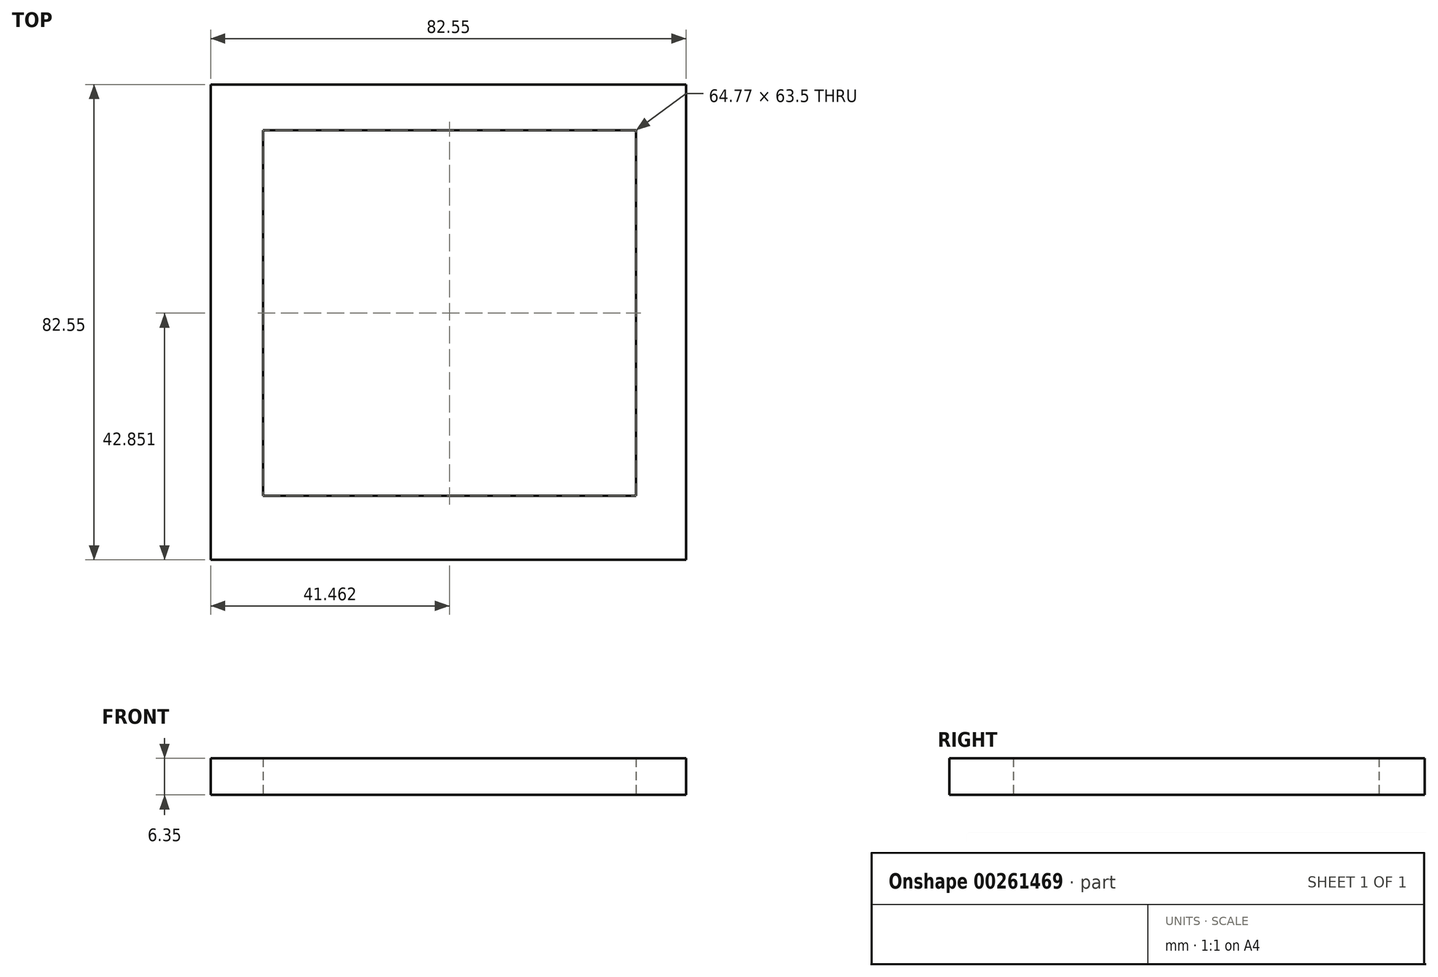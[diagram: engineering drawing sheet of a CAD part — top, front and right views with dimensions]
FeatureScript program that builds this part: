
annotation { "Feature Type Name" : "Feature", "Feature Type Description" : "" }
export const myFeature = defineFeature(function(context is Context, id is Id, definition is map)
    precondition{}
    {
        {
            var Q0;
            Q0=qCreatedBy(makeId("Top.planeOp"),FACE);
            var sketch = newSketch(context, id + "F0", { "sketchPlane" : qUnion([Q0])});
            skLineSegment(sketch, "E0.bottom", {"start": v(-56.85, 44.16) * mm, "end": v(25.7, 44.16) * mm});
            skLineSegment(sketch, "E0.top", {"start": v(-56.85, -38.4) * mm, "end": v(25.7, -38.4) * mm});
            skLineSegment(sketch, "E0.left", {"start": v(-56.85, 44.16) * mm, "end": v(-56.85, -38.4) * mm});
            skLineSegment(sketch, "E0.right", {"start": v(25.7, 44.16) * mm, "end": v(25.7, -38.4) * mm});
            skSolve(sketch);
        }
        {
            var Q0;
            Q0=makeQuery(id+"F0.imprint","IMPRINT",FACE,{"disambiguationData":[TD([[makeQuery(id+"F0.imprint","IMPRINT",EDGE,{"derivedFrom":sQuery(id+"F0.wireOp",EDGE,"E0.bottom")}),-1.0]])]});
            var sketch = newSketch(context, id + "F1", { "sketchPlane" : qUnion([Q0])});
            skLineSegment(sketch, "E1.bottom", {"start": v(-47.77, 36.21) * mm, "end": v(17, 36.21) * mm});
            skLineSegment(sketch, "E1.top", {"start": v(-47.77, -27.29) * mm, "end": v(17, -27.29) * mm});
            skLineSegment(sketch, "E1.left", {"start": v(-47.77, 36.21) * mm, "end": v(-47.77, -27.29) * mm});
            skLineSegment(sketch, "E1.right", {"start": v(17, 36.21) * mm, "end": v(17, -27.29) * mm});
            skSolve(sketch);
        }
        {
            var Q0;
            Q0 = qSketchRegion(id + "F0", true);
            extrude(context, id + "F2", {"entities" : qUnion([Q0]), "depth" : 6.35 * mm});
        }
        {
            var Q0;
            Q0=makeQuery(id+"F1.imprint","IMPRINT",FACE,{"disambiguationData":[TD([[makeQuery(id+"F1.imprint","IMPRINT",EDGE,{"derivedFrom":sQuery(id+"F1.wireOp",EDGE,"E1.bottom")}),-1.0]])]});
            extrude(context, id + "F3", {"entities" : qUnion([Q0]), "operationType" : NewBodyOperationType.REMOVE, "depth" : 24.64 * mm});
        }
    });
